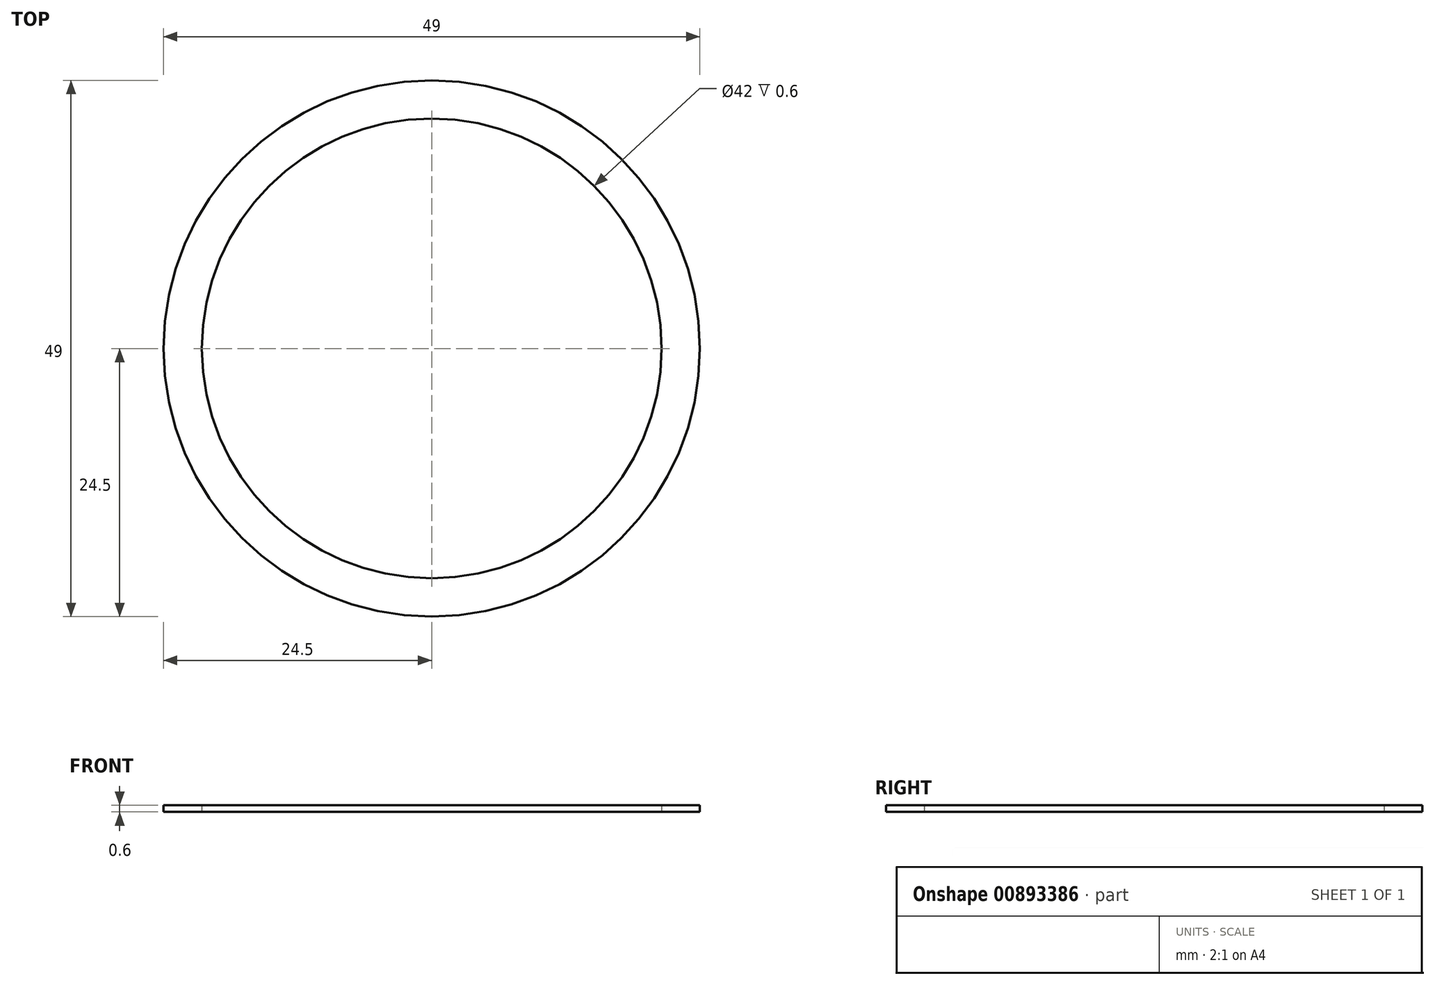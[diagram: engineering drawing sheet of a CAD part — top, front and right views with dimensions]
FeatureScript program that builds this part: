
annotation { "Feature Type Name" : "Feature", "Feature Type Description" : "" }
export const myFeature = defineFeature(function(context is Context, id is Id, definition is map)
    precondition{}
    {
        {
            var Q0;
            Q0=qCreatedBy(makeId("Top.planeOp"),FACE);
            var sketch = newSketch(context, id + "F0", { "sketchPlane" : qUnion([Q0])});
            skCircle(sketch, "E0", {"center": v(0, 0) * mm, "radius": 24.5 * mm});
            skCircle(sketch, "E1", {"center": v(0, 0) * mm, "radius": 21 * mm});
            skSolve(sketch);
        }
        {
            var Q0;
            Q0=makeQuery(id+"F0.imprint","IMPRINT",FACE,{"disambiguationData":[TD([[makeQuery(id+"F0.imprint","IMPRINT",EDGE,{"derivedFrom":sQuery(id+"F0.wireOp",EDGE,"E0")}),1.0]])]});
            extrude(context, id + "F1", {"entities" : qUnion([Q0]), "depth" : 0.6 * mm, "offsetDistance" : 25 * mm});
        }
    });
